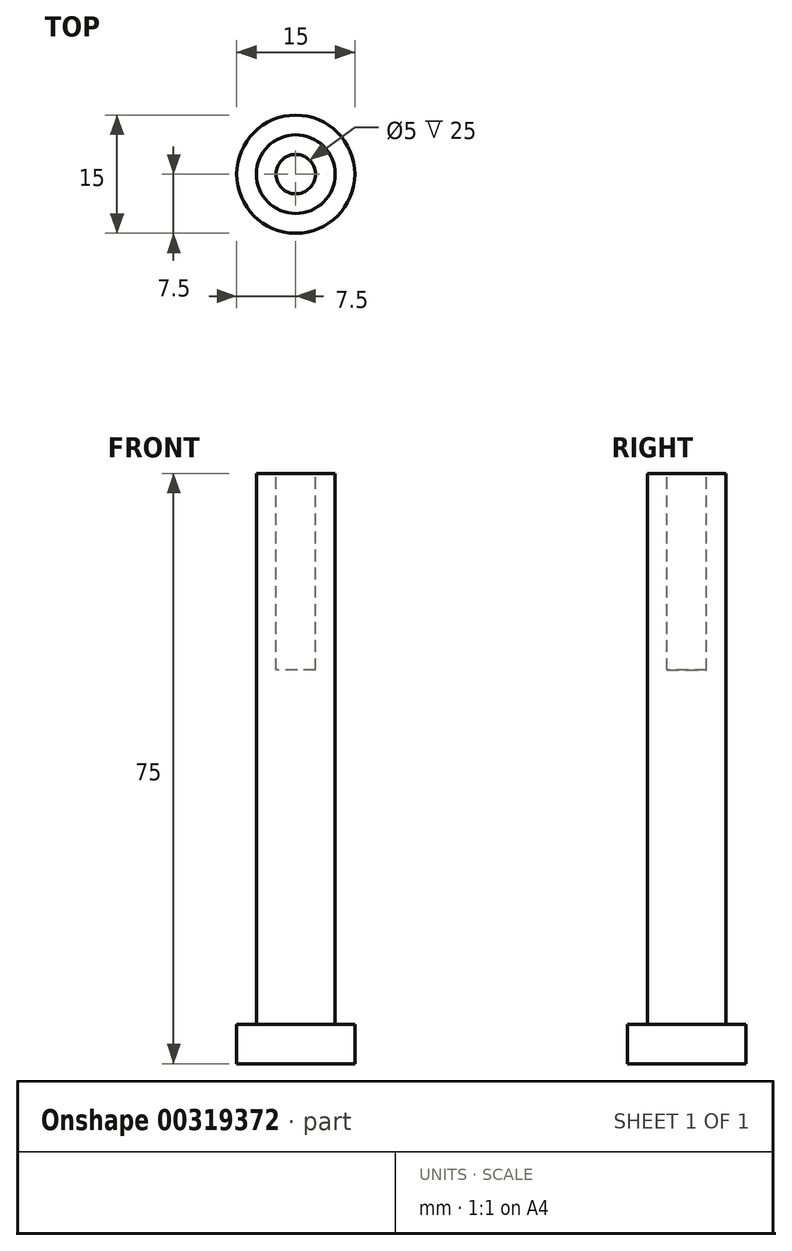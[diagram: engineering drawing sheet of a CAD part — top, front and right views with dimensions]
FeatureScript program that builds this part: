
annotation { "Feature Type Name" : "Feature", "Feature Type Description" : "" }
export const myFeature = defineFeature(function(context is Context, id is Id, definition is map)
    precondition{}
    {
        {
            var Q0;
            Q0=qCreatedBy(makeId("Top.planeOp"),FACE);
            var sketch = newSketch(context, id + "F0", { "sketchPlane" : qUnion([Q0])});
            skCircle(sketch, "E0", {"center": v(0, 0) * mm, "radius": 5 * mm});
            skSolve(sketch);
        }
        {
            var Q0;
            Q0 = qSketchRegion(id + "F0", true);
            extrude(context, id + "F1", {"entities" : qUnion([Q0]), "depth" : 70 * mm});
        }
        {
            var Q0;
            Q0=makeQuery(id+"F1.opExtrude","CAP_FACE",FACE,{"disambiguationData":[OSD([sQuery(id+"F0.wireOp",EDGE,"E0")])],"isStart":true});
            var sketch = newSketch(context, id + "F2", { "sketchPlane" : qUnion([Q0])});
            skCircle(sketch, "E1", {"center": v(0, 0) * mm, "radius": 7.5 * mm});
            skSolve(sketch);
        }
        {
            var Q0;
            Q0=makeQuery(id+"F2.imprint","IMPRINT",FACE,{"disambiguationData":[TD([[makeQuery(id+"F2.imprint","IMPRINT",EDGE,{"derivedFrom":sQuery(id+"F2.wireOp",EDGE,"E1")}),1.0]])]});
            var Q1;
            Q1=makeQuery(id+"F2.imprint","IMPRINT",FACE,{"disambiguationData":[TD([[makeQuery(id+"F2.imprint","IMPRINT",EDGE,{"derivedFrom":makeQuery(id+"F1.opExtrude","CAP_EDGE",EDGE,{"disambiguationData":[OSD([sQuery(id+"F0.wireOp",EDGE,"E0")])],"isStart":true})}),-1.0]])]});
            extrude(context, id + "F3", {"entities" : qUnion([Q0, Q1]), "operationType" : NewBodyOperationType.ADD, "depth" : 5 * mm});
        }
        {
            var Q0;
            Q0=makeQuery(id+"F1.opExtrude","CAP_FACE",FACE,{"disambiguationData":[OSD([sQuery(id+"F0.wireOp",EDGE,"E0")])],"isStart":false});
            var sketch = newSketch(context, id + "F4", { "sketchPlane" : qUnion([Q0])});
            skCircle(sketch, "E2", {"center": v(0, 0) * mm, "radius": 2.5 * mm});
            skSolve(sketch);
        }
        {
            var Q0;
            Q0 = qSketchRegion(id + "F4", true);
            extrude(context, id + "F5", {"entities" : qUnion([Q0]), "operationType" : NewBodyOperationType.REMOVE, "oppositeDirection" : true, "depth" : 25 * mm});
        }
    });
